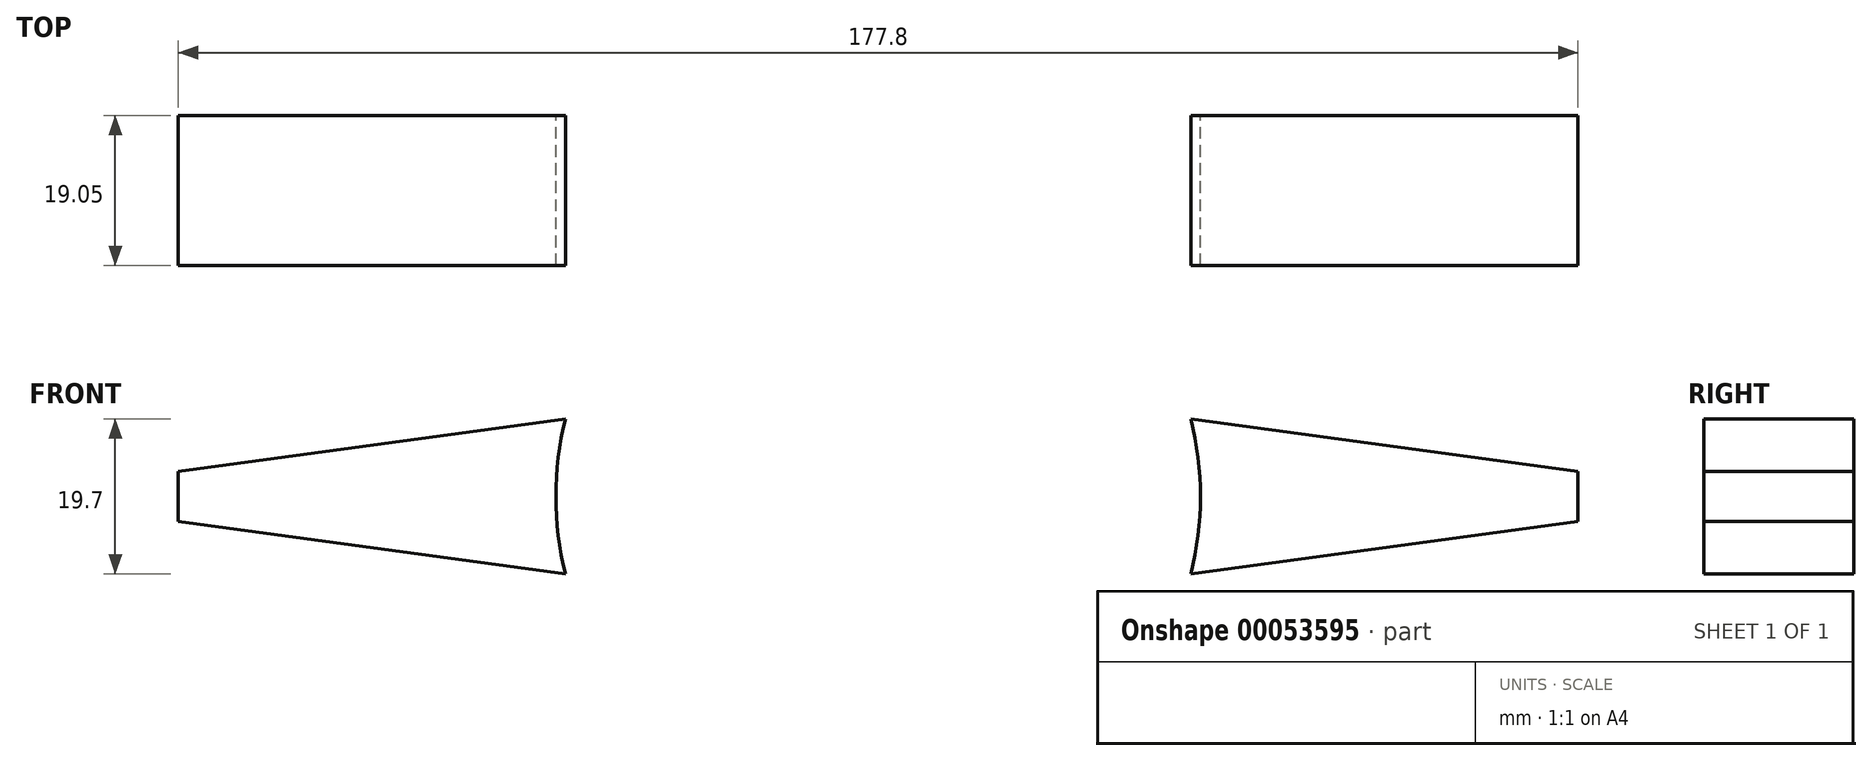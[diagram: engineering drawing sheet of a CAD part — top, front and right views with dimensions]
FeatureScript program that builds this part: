
annotation { "Feature Type Name" : "Feature", "Feature Type Description" : "" }
export const myFeature = defineFeature(function(context is Context, id is Id, definition is map)
    precondition{}
    {
        {
            var Q0;
            Q0=qCreatedBy(makeId("Front.planeOp"),FACE);
            var sketch = newSketch(context, id + "F0", { "sketchPlane" : qUnion([Q0])});
            skArc(sketch, "E0", {"start": v(-39.73, 9.85) * mm, "mid": v(-40.93, 0) * mm, "end": v(-39.73, -9.85) * mm});
            skLineSegment(sketch, "E1", {"start": v(0, 0) * mm, "end": v(0, 3.18) * mm});
            skLineSegment(sketch, "E2.right", {"start": v(-88.9, -3.18) * mm, "end": v(-88.9, 3.17) * mm});
            skLineSegment(sketch, "E3.right", {"start": v(88.9, -3.17) * mm, "end": v(88.9, 3.18) * mm});
            skLineSegment(sketch, "E4", {"start": v(-39.73, -9.85) * mm, "end": v(-88.9, -3.18) * mm});
            skLineSegment(sketch, "E5", {"start": v(-39.73, 9.85) * mm, "end": v(-88.9, 3.18) * mm});
            skLineSegment(sketch, "E6", {"start": v(39.73, 9.85) * mm, "end": v(88.9, 3.18) * mm});
            skLineSegment(sketch, "E7", {"start": v(39.73, -9.85) * mm, "end": v(88.9, -3.18) * mm});
            skArc(sketch, "E8.trimOffspring", {"start": v(39.73, -9.85) * mm, "mid": v(40.93, 0) * mm, "end": v(39.73, 9.85) * mm});
            skSolve(sketch);
        }
        {
            var Q0;
            Q0=makeQuery(id+"F0.imprint","IMPRINT",FACE,{"disambiguationData":[TD([[makeQuery(id+"F0.imprint","IMPRINT",EDGE,{"derivedFrom":sQuery(id+"F0.wireOp",EDGE,"E0")}),-1.0]])]});
            var Q1;
            Q1=makeQuery(id+"F0.imprint","IMPRINT",FACE,{"disambiguationData":[TD([[makeQuery(id+"F0.imprint","IMPRINT",EDGE,{"derivedFrom":sQuery(id+"F0.wireOp",EDGE,"E3.right")}),1.0]])]});
            extrude(context, id + "F1", {"entities" : qUnion([Q0, Q1]), "offsetDistance" : 25.4 * mm, "depth" : 19.05 * mm});
        }
    });
